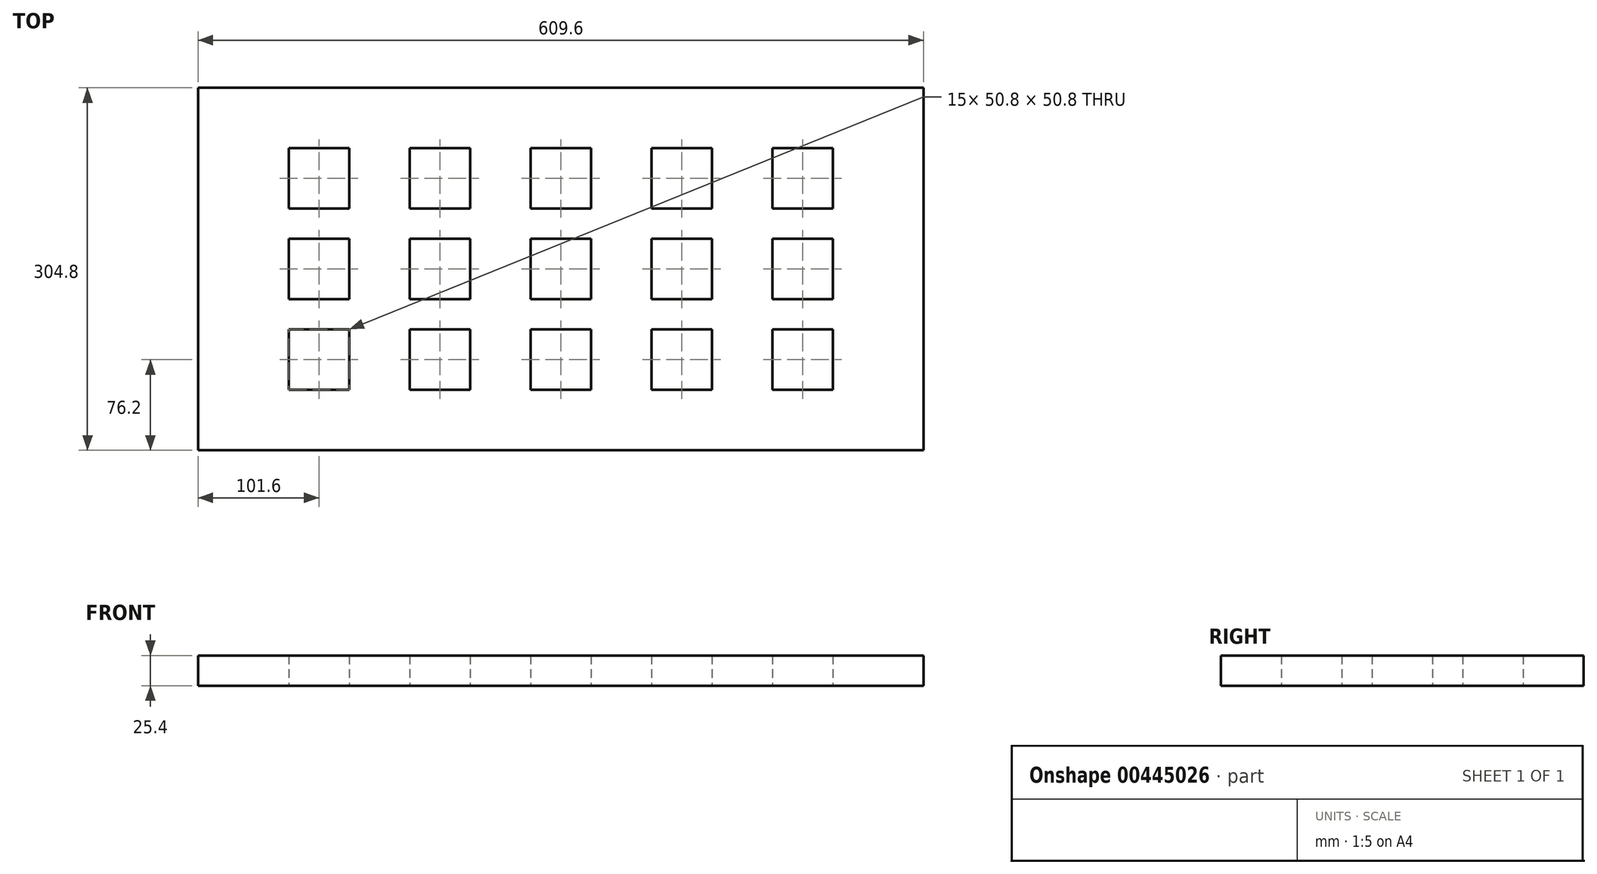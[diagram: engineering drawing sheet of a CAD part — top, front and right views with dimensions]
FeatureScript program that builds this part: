
annotation { "Feature Type Name" : "Feature", "Feature Type Description" : "" }
export const myFeature = defineFeature(function(context is Context, id is Id, definition is map)
    precondition{}
    {
        {
            var Q0;
            Q0=qCreatedBy(makeId("Top.planeOp"),FACE);
            var sketch = newSketch(context, id + "F0", { "sketchPlane" : qUnion([Q0])});
            skLineSegment(sketch, "E0.bottom", {"start": v(0, 0) * mm, "end": v(609.6, 0) * mm});
            skLineSegment(sketch, "E0.top", {"start": v(0, 304.8) * mm, "end": v(609.6, 304.8) * mm});
            skLineSegment(sketch, "E0.left", {"start": v(0, 0) * mm, "end": v(0, 304.8) * mm});
            skLineSegment(sketch, "E0.right", {"start": v(609.6, 0) * mm, "end": v(609.6, 304.8) * mm});
            skLineSegment(sketch, "E1.bottom", {"start": v(76.2, 254) * mm, "end": v(127, 254) * mm});
            skLineSegment(sketch, "E1.top", {"start": v(76.2, 203.2) * mm, "end": v(127, 203.2) * mm});
            skLineSegment(sketch, "E1.left", {"start": v(76.2, 254) * mm, "end": v(76.2, 203.2) * mm});
            skLineSegment(sketch, "E1.right", {"start": v(127, 254) * mm, "end": v(127, 203.2) * mm});
            skLineSegment(sketch, "E2.bottom", {"start": v(76.2, 177.8) * mm, "end": v(127, 177.8) * mm});
            skLineSegment(sketch, "E2.top", {"start": v(76.2, 127) * mm, "end": v(127, 127) * mm});
            skLineSegment(sketch, "E2.left", {"start": v(76.2, 177.8) * mm, "end": v(76.2, 127) * mm});
            skLineSegment(sketch, "E2.right", {"start": v(127, 177.8) * mm, "end": v(127, 127) * mm});
            skLineSegment(sketch, "E3.bottom", {"start": v(76.2, 101.6) * mm, "end": v(127, 101.6) * mm});
            skLineSegment(sketch, "E3.top", {"start": v(76.2, 50.8) * mm, "end": v(127, 50.8) * mm});
            skLineSegment(sketch, "E3.left", {"start": v(76.2, 101.6) * mm, "end": v(76.2, 50.8) * mm});
            skLineSegment(sketch, "E3.right", {"start": v(127, 101.6) * mm, "end": v(127, 50.8) * mm});
            skLineSegment(sketch, "E4.bottom", {"start": v(177.8, 254) * mm, "end": v(228.6, 254) * mm});
            skLineSegment(sketch, "E4.top", {"start": v(177.8, 203.2) * mm, "end": v(228.6, 203.2) * mm});
            skLineSegment(sketch, "E4.left", {"start": v(177.8, 254) * mm, "end": v(177.8, 203.2) * mm});
            skLineSegment(sketch, "E4.right", {"start": v(228.6, 254) * mm, "end": v(228.6, 203.2) * mm});
            skLineSegment(sketch, "E5.bottom", {"start": v(279.4, 254) * mm, "end": v(330.2, 254) * mm});
            skLineSegment(sketch, "E5.top", {"start": v(279.4, 203.2) * mm, "end": v(330.2, 203.2) * mm});
            skLineSegment(sketch, "E5.left", {"start": v(330.2, 254) * mm, "end": v(330.2, 203.2) * mm});
            skLineSegment(sketch, "E5.right", {"start": v(279.4, 254) * mm, "end": v(279.4, 203.2) * mm});
            skLineSegment(sketch, "E6.bottom", {"start": v(381, 254) * mm, "end": v(431.8, 254) * mm});
            skLineSegment(sketch, "E6.top", {"start": v(381, 203.2) * mm, "end": v(431.8, 203.2) * mm});
            skLineSegment(sketch, "E6.left", {"start": v(381, 254) * mm, "end": v(381, 203.2) * mm});
            skLineSegment(sketch, "E6.right", {"start": v(431.8, 254) * mm, "end": v(431.8, 203.2) * mm});
            skLineSegment(sketch, "E7.bottom", {"start": v(482.6, 254) * mm, "end": v(533.4, 254) * mm});
            skLineSegment(sketch, "E7.top", {"start": v(482.6, 203.2) * mm, "end": v(533.4, 203.2) * mm});
            skLineSegment(sketch, "E7.left", {"start": v(482.6, 254) * mm, "end": v(482.6, 203.2) * mm});
            skLineSegment(sketch, "E7.right", {"start": v(533.4, 254) * mm, "end": v(533.4, 203.2) * mm});
            skLineSegment(sketch, "E8.bottom", {"start": v(177.8, 177.8) * mm, "end": v(228.6, 177.8) * mm});
            skLineSegment(sketch, "E8.top", {"start": v(177.8, 127) * mm, "end": v(228.6, 127) * mm});
            skLineSegment(sketch, "E8.left", {"start": v(177.8, 177.8) * mm, "end": v(177.8, 127) * mm});
            skLineSegment(sketch, "E8.right", {"start": v(228.6, 177.8) * mm, "end": v(228.6, 127) * mm});
            skLineSegment(sketch, "E9.bottom", {"start": v(279.4, 177.8) * mm, "end": v(330.2, 177.8) * mm});
            skLineSegment(sketch, "E9.top", {"start": v(279.4, 127) * mm, "end": v(330.2, 127) * mm});
            skLineSegment(sketch, "E9.left", {"start": v(279.4, 177.8) * mm, "end": v(279.4, 127) * mm});
            skLineSegment(sketch, "E9.right", {"start": v(330.2, 177.8) * mm, "end": v(330.2, 127) * mm});
            skLineSegment(sketch, "E10.bottom", {"start": v(381, 177.8) * mm, "end": v(431.8, 177.8) * mm});
            skLineSegment(sketch, "E10.top", {"start": v(381, 127) * mm, "end": v(431.8, 127) * mm});
            skLineSegment(sketch, "E10.left", {"start": v(381, 177.8) * mm, "end": v(381, 127) * mm});
            skLineSegment(sketch, "E10.right", {"start": v(431.8, 177.8) * mm, "end": v(431.8, 127) * mm});
            skLineSegment(sketch, "E11.bottom", {"start": v(482.6, 177.8) * mm, "end": v(533.4, 177.8) * mm});
            skLineSegment(sketch, "E11.top", {"start": v(482.6, 127) * mm, "end": v(533.4, 127) * mm});
            skLineSegment(sketch, "E11.left", {"start": v(482.6, 177.8) * mm, "end": v(482.6, 127) * mm});
            skLineSegment(sketch, "E11.right", {"start": v(533.4, 177.8) * mm, "end": v(533.4, 127) * mm});
            skLineSegment(sketch, "E12.bottom", {"start": v(177.8, 101.6) * mm, "end": v(228.6, 101.6) * mm});
            skLineSegment(sketch, "E12.top", {"start": v(177.8, 50.8) * mm, "end": v(228.6, 50.8) * mm});
            skLineSegment(sketch, "E12.left", {"start": v(177.8, 101.6) * mm, "end": v(177.8, 50.8) * mm});
            skLineSegment(sketch, "E12.right", {"start": v(228.6, 101.6) * mm, "end": v(228.6, 50.8) * mm});
            skLineSegment(sketch, "E13.bottom", {"start": v(279.4, 101.6) * mm, "end": v(330.2, 101.6) * mm});
            skLineSegment(sketch, "E13.top", {"start": v(279.4, 50.8) * mm, "end": v(330.2, 50.8) * mm});
            skLineSegment(sketch, "E13.left", {"start": v(279.4, 101.6) * mm, "end": v(279.4, 50.8) * mm});
            skLineSegment(sketch, "E13.right", {"start": v(330.2, 101.6) * mm, "end": v(330.2, 50.8) * mm});
            skLineSegment(sketch, "E14.bottom", {"start": v(381, 101.6) * mm, "end": v(431.8, 101.6) * mm});
            skLineSegment(sketch, "E14.top", {"start": v(381, 50.8) * mm, "end": v(431.8, 50.8) * mm});
            skLineSegment(sketch, "E14.left", {"start": v(381, 101.6) * mm, "end": v(381, 50.8) * mm});
            skLineSegment(sketch, "E14.right", {"start": v(431.8, 101.6) * mm, "end": v(431.8, 50.8) * mm});
            skLineSegment(sketch, "E15.bottom", {"start": v(482.6, 101.6) * mm, "end": v(533.4, 101.6) * mm});
            skLineSegment(sketch, "E15.top", {"start": v(482.6, 50.8) * mm, "end": v(533.4, 50.8) * mm});
            skLineSegment(sketch, "E15.left", {"start": v(482.6, 101.6) * mm, "end": v(482.6, 50.8) * mm});
            skLineSegment(sketch, "E15.right", {"start": v(533.4, 101.6) * mm, "end": v(533.4, 50.8) * mm});
            skLineSegment(sketch, "E16", {"start": v(304.8, 304.8) * mm, "end": v(304.8, 0) * mm, "construction": true});
            skPoint(sketch, "E17", {"position": v(304.8, 254) * mm});
            skPoint(sketch, "E18", {"position": v(304.8, 177.8) * mm});
            skPoint(sketch, "E19", {"position": v(304.8, 101.6) * mm});
            skLineSegment(sketch, "E20", {"start": v(101.6, 304.8) * mm, "end": v(101.6, 0) * mm, "construction": true});
            skLineSegment(sketch, "E21", {"start": v(203.2, 304.8) * mm, "end": v(203.2, 0) * mm, "construction": true});
            skLineSegment(sketch, "E22", {"start": v(406.4, 304.8) * mm, "end": v(406.4, 0) * mm, "construction": true});
            skLineSegment(sketch, "E23", {"start": v(508, 304.8) * mm, "end": v(508, 0) * mm, "construction": true});
            skPoint(sketch, "E23.startSnap0", {"position": v(508, 254) * mm});
            skPoint(sketch, "E23.endSnap0", {"position": v(508, 254) * mm});
            skPoint(sketch, "E24", {"position": v(101.6, 254) * mm});
            skPoint(sketch, "E25", {"position": v(101.6, 177.8) * mm});
            skPoint(sketch, "E26", {"position": v(101.6, 101.6) * mm});
            skPoint(sketch, "E27", {"position": v(203.2, 254) * mm});
            skPoint(sketch, "E28", {"position": v(203.2, 177.8) * mm});
            skPoint(sketch, "E29", {"position": v(203.2, 101.6) * mm});
            skPoint(sketch, "E30", {"position": v(406.4, 254) * mm});
            skPoint(sketch, "E31", {"position": v(406.4, 177.8) * mm});
            skPoint(sketch, "E32", {"position": v(406.4, 101.6) * mm});
            skPoint(sketch, "E33", {"position": v(508, 101.6) * mm});
            skPoint(sketch, "E34", {"position": v(508, 177.8) * mm});
            skLineSegment(sketch, "E35", {"start": v(0, 228.6) * mm, "end": v(609.6, 228.6) * mm, "construction": true});
            skPoint(sketch, "E35.startSnap0", {"position": v(76.2, 228.6) * mm});
            skLineSegment(sketch, "E36", {"start": v(0, 152.4) * mm, "end": v(609.6, 152.4) * mm, "construction": true});
            skLineSegment(sketch, "E37", {"start": v(0, 76.2) * mm, "end": v(609.6, 76.2) * mm, "construction": true});
            skPoint(sketch, "E38", {"position": v(177.8, 228.6) * mm});
            skPoint(sketch, "E39", {"position": v(279.4, 228.6) * mm});
            skPoint(sketch, "E40", {"position": v(381, 228.6) * mm});
            skPoint(sketch, "E41", {"position": v(482.6, 228.6) * mm});
            skPoint(sketch, "E42", {"position": v(482.6, 152.4) * mm});
            skPoint(sketch, "E43", {"position": v(381, 152.4) * mm});
            skPoint(sketch, "E44", {"position": v(279.4, 152.4) * mm});
            skPoint(sketch, "E45", {"position": v(177.8, 152.4) * mm});
            skPoint(sketch, "E46", {"position": v(76.2, 152.4) * mm});
            skPoint(sketch, "E47", {"position": v(76.2, 76.2) * mm});
            skPoint(sketch, "E48", {"position": v(177.8, 76.2) * mm});
            skPoint(sketch, "E49", {"position": v(279.4, 76.2) * mm});
            skPoint(sketch, "E50", {"position": v(381, 76.2) * mm});
            skPoint(sketch, "E51", {"position": v(482.6, 76.2) * mm});
            skSolve(sketch);
        }
        {
            var Q0;
            Q0=makeQuery(id+"F0.imprint","IMPRINT",FACE,{"disambiguationData":[TD([[makeQuery(id+"F0.imprint","IMPRINT",EDGE,{"derivedFrom":sQuery(id+"F0.wireOp",EDGE,"E0.bottom")}),1.0]])]});
            extrude(context, id + "F1", {"entities" : qUnion([Q0]), "depth" : 3.17 * mm});
        }
        {
            var Q0;
            Q0 = qSketchRegion(id + "F0", true);
            extrude(context, id + "F2", {"entities" : qUnion([Q0]), "operationType" : NewBodyOperationType.ADD, "depth" : 25.4 * mm});
        }
    });
